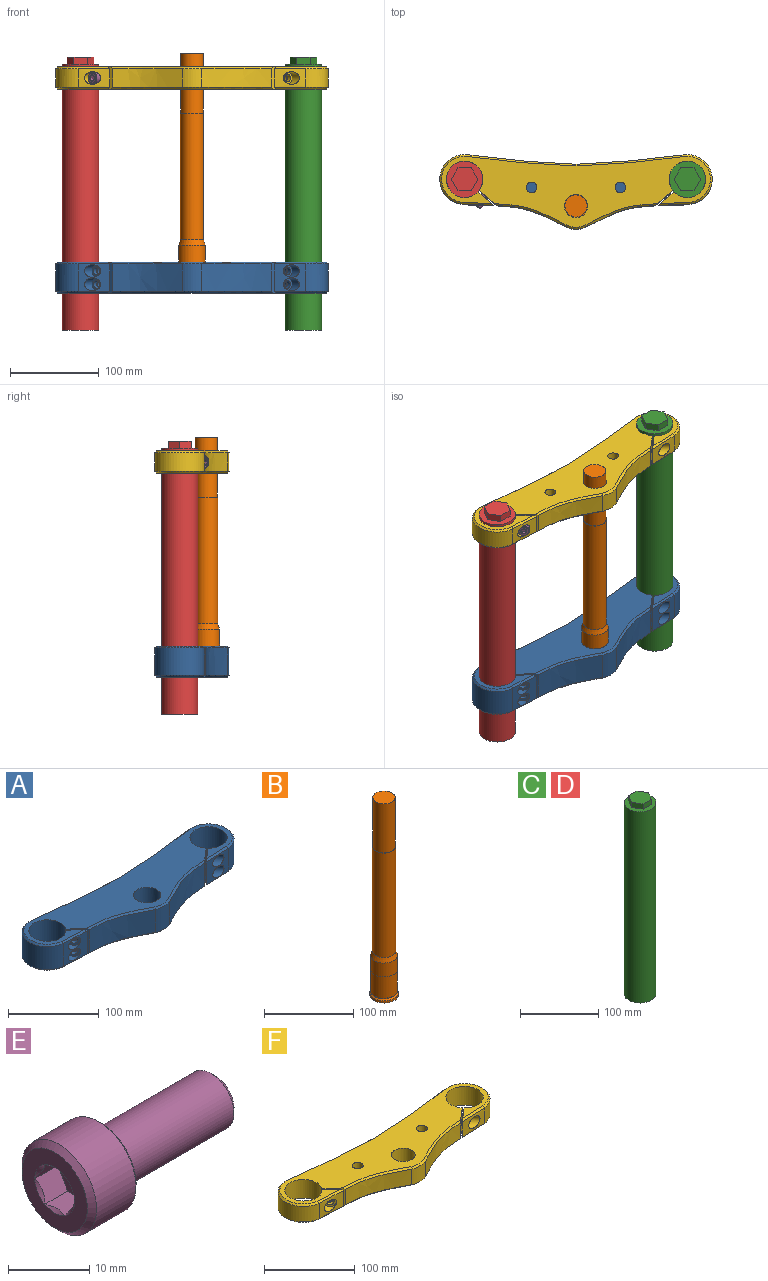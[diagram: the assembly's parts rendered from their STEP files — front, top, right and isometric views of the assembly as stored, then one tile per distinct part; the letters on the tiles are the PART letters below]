
ASSEMBLY  parts=6 mates=10
PART A: 58 faces, bbox 309.2x86.9x37.2 mm
  f0: extruded ~35.76x31mm, area 701.9mm2, adj f4,f5,f10,f17,f22,f27
  f1: extruded ~78.62x31mm, area 2580.8mm2, adj f2,f7,f14,f15
  f2: cylinder r=26mm len=31mm, axis (0,0,-1), area 696.4mm2, adj f1,f13,f14,f15,f16,f31,f40,f41
  f3: extruded ~122.86x31mm, area 3825mm2, adj f4,f12,f19,f32
  f4: cylinder r=28mm len=55.84mm, axis (0,0,-1), area 2716.9mm2, adj f0,f3,f11,f12,f18,f19
  f5: plane 35.01x17.87mm, normal (0.65,0.76,0), area 688.3mm2, adj f0,f6,f8,f9,f10,f17,f23,f28
  f6: cylinder r=20.5mm len=41mm, axis (0,0,-1), area 4438.2mm2, adj f5,f7,f8,f9
  f7: plane 35.01x19.78mm, normal (-0.65,-0.76,0), area 776.2mm2, adj f1,f6,f8,f9,f14,f15,f21,f26
  f8: plane 305.19x82.19mm, normal (0,0,1), area 12284.8mm2, adj f5,f6,f7,f15,f16,f17,f18,f19
  f9: plane 305.19x82.19mm, normal (0,0,-1), area 12192.2mm2, adj f5,f6,f7,f10,f11,f12,f13,f14
  f10: bspline ~39.38x3.7mm, area 97.4mm2, adj f0,f5,f9,f11
  f11: cone r=28mm half-angle=45deg, axis (0,0,1), area 238.8mm2, adj f4,f9,f10,f12
  f12: bspline ~135.45x13.66mm, area 349.3mm2, adj f3,f4,f9,f11,f39
  f13: cone r=26mm half-angle=45deg, axis (0,0,1), area 60.8mm2, adj f2,f9,f14,f40
  f14: bspline ~90.23x28.35mm, area 240.3mm2, adj f1,f2,f7,f9,f13
  f15: bspline ~90.23x28.35mm, area 240.3mm2, adj f1,f2,f7,f8,f16
  f16: cone r=24mm half-angle=45deg, axis (0,0,-1), area 60.7mm2, adj f2,f8,f15,f41
  f17: bspline ~39.38x3.7mm, area 97.4mm2, adj f0,f5,f8,f18
  f18: cone r=26mm half-angle=45deg, axis (0,0,-1), area 239mm2, adj f4,f8,f17,f19
  f19: bspline ~135.45x13.66mm, area 349.3mm2, adj f3,f4,f8,f18,f44
  f20: cone r=0mm half-angle=59deg, axis (-0.65,-0.76,0), area 74.2mm2, adj f21
  f21: cylinder r=4.5mm len=9mm, axis (-0.65,-0.76,0), area 91.9mm2, adj f7,f20
  f22: cylinder r=7.12mm len=19.11mm, axis (-0.65,-0.76,0), area 319.5mm2, adj f0,f24
  f23: cylinder r=4.5mm len=10.09mm, axis (-0.65,-0.76,0), area 141.4mm2, adj f5,f24
  f24: plane 14.25x10.84mm, normal (-0.65,-0.76,0), area 95.9mm2, adj f22,f23
  f25: cone r=0mm half-angle=59deg, axis (-0.65,-0.76,0), area 74.2mm2, adj f26
  f26: cylinder r=4.5mm len=9mm, axis (-0.65,-0.76,0), area 91.9mm2, adj f7,f25
  f27: cylinder r=7.12mm len=19.11mm, axis (-0.65,-0.76,0), area 319.5mm2, adj f0,f29
  f28: cylinder r=4.5mm len=10.09mm, axis (-0.65,-0.76,0), area 141.4mm2, adj f5,f29
  f29: plane 14.25x10.84mm, normal (-0.65,-0.76,0), area 95.9mm2, adj f27,f28
  f30: extruded ~35.76x31mm, area 701.9mm2, adj f33,f34,f37,f42,f47,f52
  f31: extruded ~78.62x31mm, area 2580.8mm2, adj f2,f36,f40,f41
  f32: extruded ~122.86x31mm, area 3825mm2, adj f3,f33,f39,f44
  f33: cylinder r=28mm len=55.84mm, axis (0,0,-1), area 2716.6mm2, adj f30,f32,f38,f39,f43,f44
  f34: plane 35.01x17.87mm, normal (-0.65,0.76,0), area 688.3mm2, adj f8,f9,f30,f35,f37,f42,f48,f53
  f35: cylinder r=20.5mm len=41mm, axis (0,0,-1), area 4438.2mm2, adj f8,f9,f34,f36
  f36: plane 35.01x19.78mm, normal (0.65,-0.76,0), area 776.2mm2, adj f8,f9,f31,f35,f40,f41,f46,f51
  f37: bspline ~39.38x3.7mm, area 97.5mm2, adj f9,f30,f34,f38
  f38: cone r=28mm half-angle=45deg, axis (0,0,1), area 239mm2, adj f9,f33,f37,f39
  f39: bspline ~135.45x13.66mm, area 349.4mm2, adj f9,f12,f32,f33,f38
  f40: bspline ~90.23x28.35mm, area 240.4mm2, adj f2,f9,f13,f31,f36
  f41: bspline ~90.23x28.35mm, area 240.4mm2, adj f2,f8,f16,f31,f36
  f42: bspline ~39.38x3.7mm, area 97.5mm2, adj f8,f30,f34,f43
  f43: cone r=26mm half-angle=45deg, axis (0,0,-1), area 238.7mm2, adj f8,f33,f42,f44
  f44: bspline ~135.45x13.66mm, area 349.4mm2, adj f8,f19,f32,f33,f43
  f45: cone r=0mm half-angle=59deg, axis (0.65,-0.76,0), area 74.2mm2, adj f46
  f46: cylinder r=4.5mm len=9mm, axis (0.65,-0.76,0), area 91.9mm2, adj f36,f45
  f47: cylinder r=7.12mm len=19.11mm, axis (0.65,-0.76,0), area 319.5mm2, adj f30,f49
  f48: cylinder r=4.5mm len=10.09mm, axis (0.65,-0.76,0), area 141.4mm2, adj f34,f49
  f49: plane 14.25x10.84mm, normal (0.65,-0.76,0), area 95.9mm2, adj f47,f48
  f50: cone r=0mm half-angle=59deg, axis (0.65,-0.76,0), area 74.2mm2, adj f51
  f51: cylinder r=4.5mm len=9mm, axis (0.65,-0.76,0), area 91.9mm2, adj f36,f50
  f52: cylinder r=7.12mm len=19.11mm, axis (0.65,-0.76,0), area 319.5mm2, adj f30,f54
  f53: cylinder r=4.5mm len=10.09mm, axis (0.65,-0.76,0), area 141.4mm2, adj f34,f54
  f54: plane 14.25x10.84mm, normal (0.65,-0.76,0), area 95.9mm2, adj f52,f53
  f55: cylinder r=15mm len=31mm, axis (0,0,-1), area 2921.7mm2, adj f8,f56
  f56: cone r=16mm half-angle=45deg, axis (0,0,-1), area 137.7mm2, adj f55,f57
  f57: cylinder r=16mm len=32mm, axis (0,0,-1), area 301.6mm2, adj f9,f56
PART B: 13 faces, bbox 32x32x270 mm
  f0: cylinder r=14.47mm len=28.93mm, axis (0,0,1), area 67.1mm2, adj f1,f12
  f1: cone r=14.47mm half-angle=45deg, axis (0,0,-1), area 207.5mm2, adj f0,f2
  f2: cylinder r=16mm len=32mm, axis (0,0,1), area 301.6mm2, adj f1,f3
  f3: plane 32x32mm, normal (0,0,-1), area 804.2mm2, adj f2
  f4: plane 25x25mm, normal (0,0,1), area 490.9mm2, adj f5
  f5: cylinder r=12.5mm len=67mm, axis (0,0,1), area 5262.2mm2, adj f4,f6
  f6: plane 26x26mm, normal (0,0,1), area 40.1mm2, adj f5,f7
  f7: cylinder r=13mm len=143mm, axis (0,0,1), area 11680.4mm2, adj f6,f8
  f8: cone r=13mm half-angle=18.4deg, axis (0,0,-1), area 558.7mm2, adj f7,f9
  f9: cylinder r=15mm len=30mm, axis (0,0,1), area 1788.1mm2, adj f8,f10
  f10: plane 30.01x30.01mm, normal (0,0,1), area 0.2mm2, adj f9,f11
  f11: cylinder r=15mm len=30.01mm, axis (0,0,1), area 2751.9mm2, adj f10,f12
  f12: cone r=14.47mm half-angle=45deg, axis (0,0,1), area 70.1mm2, adj f0,f11
PART C: 10 faces, bbox 41x41x308 mm
  f0: plane 41x41mm, normal (0,0,1), area 733.6mm2, adj f1,f3,f4,f5,f6,f7,f8
  f1: cylinder r=20.5mm len=300mm, axis (0,0,-1), area 38641.6mm2, adj f0,f2
  f2: plane 41x41mm, normal (0,0,-1), area 1320.3mm2, adj f1
  f3: plane 13.01x8mm, normal (0.87,-0.5,0), area 120.2mm2, adj f0,f4,f8,f9
  f4: plane 13.01x8mm, normal (0.87,0.5,0), area 120.2mm2, adj f0,f3,f5,f9
  f5: plane 15.03x8mm, normal (0,1,0), area 120.2mm2, adj f0,f4,f6,f9
  f6: plane 13.01x8mm, normal (-0.87,0.5,0), area 120.2mm2, adj f0,f5,f7,f9
  f7: plane 13.01x8mm, normal (-0.87,-0.5,0), area 120.2mm2, adj f0,f6,f8,f9
  f8: plane 15.03x8mm, normal (0,-1,0), area 120.2mm2, adj f0,f3,f7,f9
  f9: plane 30.05x26.03mm, normal (0,0,1), area 586.7mm2, adj f3,f4,f5,f6,f7,f8
PART D: same geometry as C
PART E: 24 faces, bbox 28x13x13 mm
  f0: cone r=3.46mm half-angle=45deg, axis (-1,0,0), area 1.5mm2, adj f16,f17
  f1: cone r=3.46mm half-angle=45deg, axis (-1,0,0), area 1.5mm2, adj f16,f18
  f2: cone r=3.46mm half-angle=45deg, axis (-1,0,0), area 1.5mm2, adj f16,f19
  f3: cone r=3.46mm half-angle=45deg, axis (-1,0,0), area 1.5mm2, adj f16,f20
  f4: cone r=3.46mm half-angle=45deg, axis (-1,0,0), area 1.5mm2, adj f16,f21
  f5: cone r=3.46mm half-angle=45deg, axis (-1,0,0), area 1.5mm2, adj f16,f22
  f6: plane 12.33x12.33mm, normal (1,0,0), area 52.9mm2, adj f9,f13
  f7: torus R=4.4mm, axis (1,0,0), area 3.1mm2, adj f8,f12
  f8: cone r=4.02mm half-angle=17.9deg, axis (-1,0,0), area 16.9mm2, adj f7,f9
  f9: torus R=4.6mm, axis (1,0,0), area 13.9mm2, adj f6,f8
  f10: plane 6.47x6.47mm, normal (1,0,0), area 32.8mm2, adj f11
  f11: cone r=4mm half-angle=45deg, axis (-1,0,0), area 24.6mm2, adj f10,f12
  f12: cylinder r=4mm len=18.21mm, axis (1,0,0), area 457.7mm2, adj f7,f11
  f13: cone r=6.17mm half-angle=45deg, axis (-1,0,0), area 18.9mm2, adj f6,f14
  f14: cylinder r=6.5mm len=13mm, axis (1,0,0), area 280.4mm2, adj f13,f15
  f15: cone r=6.5mm half-angle=45deg, axis (1,0,0), area 43.4mm2, adj f14,f16
  f16: plane 11.4x11.4mm, normal (-1,0,0), area 64.4mm2, adj f0,f1,f2,f3,f4,f5,f15
  f17: plane 4x3.47mm, normal (0,0,-1), area 12.8mm2, adj f0,f18,f22,f23
  f18: plane 4x3mm, normal (0,0.87,-0.5), area 12.8mm2, adj f1,f17,f19,f23
  f19: plane 4x3mm, normal (0,0.87,0.5), area 12.8mm2, adj f2,f18,f20,f23
  f20: plane 4x3.47mm, normal (0,0,1), area 12.8mm2, adj f3,f19,f21,f23
  f21: plane 4x3mm, normal (0,-0.87,0.5), area 12.8mm2, adj f4,f20,f22,f23
  f22: plane 4x3mm, normal (0,-0.87,-0.5), area 12.8mm2, adj f5,f17,f21,f23
  f23: plane 6.93x6mm, normal (-1,0,0), area 31.2mm2, adj f17,f18,f19,f20,f21,f22
PART F: 48 faces, bbox 309.2x86.9x27.2 mm
  f0: plane 305.19x82.19mm, normal (0,0,-1), area 12239.3mm2, adj f4,f5,f6,f9,f14,f15,f18,f19
  f1: extruded ~35.76x21mm, area 547.8mm2, adj f3,f4,f13,f20,f23
  f2: extruded ~122.86x21mm, area 2591.2mm2, adj f3,f11,f18,f28
  f3: cylinder r=28mm len=55.84mm, axis (0,0,-1), area 1840.7mm2, adj f1,f2,f11,f12,f18,f19
  f4: plane 25.01x17.87mm, normal (0.65,0.76,0), area 517.1mm2, adj f0,f1,f5,f10,f13,f20,f24
  f5: cylinder r=20.5mm len=41mm, axis (0,0,-1), area 3170.1mm2, adj f0,f4,f6,f10
  f6: plane 25.01x19.78mm, normal (-0.65,-0.76,0), area 579.8mm2, adj f0,f5,f7,f10,f14,f16,f22
  f7: extruded ~78.62x24.2mm, area 1748.3mm2, adj f6,f8,f14,f16
  f8: cylinder r=26mm len=21.77mm, axis (0,0,-1), area 471.8mm2, adj f7,f14,f15,f16,f17,f33,f37,f38
  f9: cylinder r=13mm len=26mm, axis (0,0,-1), area 2042mm2, adj f0,f10
  f10: plane 305.19x82.19mm, normal (0,0,1), area 12234.5mm2, adj f4,f5,f6,f9,f11,f12,f13,f16
  f11: bspline ~135.45x13.66mm, area 349.3mm2, adj f2,f3,f10,f12,f34
  f12: cone r=26mm half-angle=45deg, axis (0,0,-1), area 238.9mm2, adj f3,f10,f11,f13
  f13: bspline ~39.38x3.68mm, area 97.4mm2, adj f1,f4,f10,f12
  f14: bspline ~90.23x28.35mm, area 240.3mm2, adj f0,f6,f7,f8,f15
  f15: cone r=26mm half-angle=45deg, axis (0,0,1), area 60.7mm2, adj f0,f8,f14,f37
  f16: bspline ~90.23x28.35mm, area 240.3mm2, adj f6,f7,f8,f10,f17
  f17: cone r=24mm half-angle=45deg, axis (0,0,-1), area 60.7mm2, adj f8,f10,f16,f38
  f18: bspline ~135.45x13.66mm, area 349.3mm2, adj f0,f2,f3,f19,f39
  f19: cone r=28mm half-angle=45deg, axis (0,0,1), area 238.7mm2, adj f0,f3,f18,f20
  f20: bspline ~39.38x3.68mm, area 97.4mm2, adj f0,f1,f4,f19
  f21: cone r=0mm half-angle=59deg, axis (-0.65,-0.76,0), area 74.2mm2, adj f22
  f22: cylinder r=4.5mm len=9mm, axis (-0.65,-0.76,0), area 91.9mm2, adj f6,f21
  f23: cylinder r=7.12mm len=19.11mm, axis (-0.65,-0.76,0), area 319.5mm2, adj f1,f25
  f24: cylinder r=4.5mm len=10.09mm, axis (-0.65,-0.76,0), area 141.4mm2, adj f4,f25
  f25: plane 14.25x10.84mm, normal (-0.65,-0.76,0), area 95.9mm2, adj f23,f24
  f26: cylinder r=6mm len=25mm, axis (0,0,1), area 942.5mm2, adj f0,f10
  f27: extruded ~35.76x21mm, area 547.8mm2, adj f29,f30,f36,f41,f44
  f28: extruded ~122.86x21mm, area 2591.2mm2, adj f2,f29,f34,f39
  f29: cylinder r=28mm len=55.84mm, axis (0,0,-1), area 1840.2mm2, adj f27,f28,f34,f35,f39,f40
  f30: plane 25.01x17.87mm, normal (-0.65,0.76,0), area 517.1mm2, adj f0,f10,f27,f31,f36,f41,f45
  f31: cylinder r=20.5mm len=41mm, axis (0,0,-1), area 3170.1mm2, adj f0,f10,f30,f32
  f32: plane 25.01x19.78mm, normal (0.65,-0.76,0), area 579.8mm2, adj f0,f10,f31,f33,f37,f38,f43
  f33: extruded ~78.62x24.2mm, area 1748.3mm2, adj f8,f32,f37,f38
  f34: bspline ~135.45x13.66mm, area 349.4mm2, adj f10,f11,f28,f29,f35
  f35: cone r=26mm half-angle=45deg, axis (0,0,-1), area 238.5mm2, adj f10,f29,f34,f36
  f36: bspline ~39.38x3.68mm, area 97.5mm2, adj f10,f27,f30,f35
  f37: bspline ~90.23x28.35mm, area 240.4mm2, adj f0,f8,f15,f32,f33
  f38: bspline ~90.23x28.35mm, area 240.4mm2, adj f8,f10,f17,f32,f33
  f39: bspline ~135.45x13.66mm, area 349.4mm2, adj f0,f18,f28,f29,f40
  f40: cone r=28mm half-angle=45deg, axis (0,0,1), area 238.8mm2, adj f0,f29,f39,f41
  f41: bspline ~39.38x3.68mm, area 97.5mm2, adj f0,f27,f30,f40
  f42: cone r=0mm half-angle=59deg, axis (0.65,-0.76,0), area 74.2mm2, adj f43
  f43: cylinder r=4.5mm len=9mm, axis (0.65,-0.76,0), area 91.9mm2, adj f32,f42
  f44: cylinder r=7.12mm len=19.11mm, axis (0.65,-0.76,0), area 319.5mm2, adj f27,f46
  f45: cylinder r=4.5mm len=10.09mm, axis (0.65,-0.76,0), area 141.4mm2, adj f30,f46
  f46: plane 14.25x10.84mm, normal (0.65,-0.76,0), area 95.9mm2, adj f44,f45
  f47: cylinder r=6mm len=25mm, axis (0,0,1), area 942.5mm2, adj f0,f10
PLACE A t=(-0.05,-45.64,7.27)mm
PLACE B rot(axis=(0,0,1),89deg) t=(-0.05,-45.64,7.27)mm
PLACE C t=(125.45,-15.64,-244.73)mm
PLACE D t=(-125.55,-15.64,-244.73)mm
PLACE E rot(axis=(0,0,1),49.5deg) t=(-107.44,-38.99,39.77)mm
PLACE F rot(axis=(-0.01,-0.02,1),0deg) t=(-0.05,-45.64,27.27)mm
MATE planar F.f10 <-> B.f8  axis (0,0,1) through (-0.05,-23.11,52.27)mm
MATE cylindrical B.f0 <-> A.f2  axis (0,0,1) through (-0.05,-45.64,-158.24)mm
MATE slider A.f4 <-> D.f1  axis (0,0,-1) through (-125.55,-15.64,-167.73)mm
MATE slider C.f1 <-> F.f29  axis (0,0,-1) through (125.45,-15.64,55.27)mm
MATE planar A.f9 <-> B.f0  axis (0,0,-1) through (-0.05,-22.63,-202.73)mm
MATE planar F.f10 <-> D.f1  axis (0,0,1) through (-0.05,-23.11,52.27)mm
MATE slider D.f1 <-> F.f3  axis (0,0,-1) through (-125.55,-15.64,55.27)mm
MATE planar E.f0 <-> F.f21  axis (0.65,0.76,0) through (-107.44,-38.99,39.77)mm
MATE planar C.f1 <-> D.f1  axis (0,0,-1) through (125.45,-15.64,55.27)mm
MATE slider E.f0 <-> F.f21  axis (0.65,0.76,0) through (-112.11,-44.47,39.77)mm
